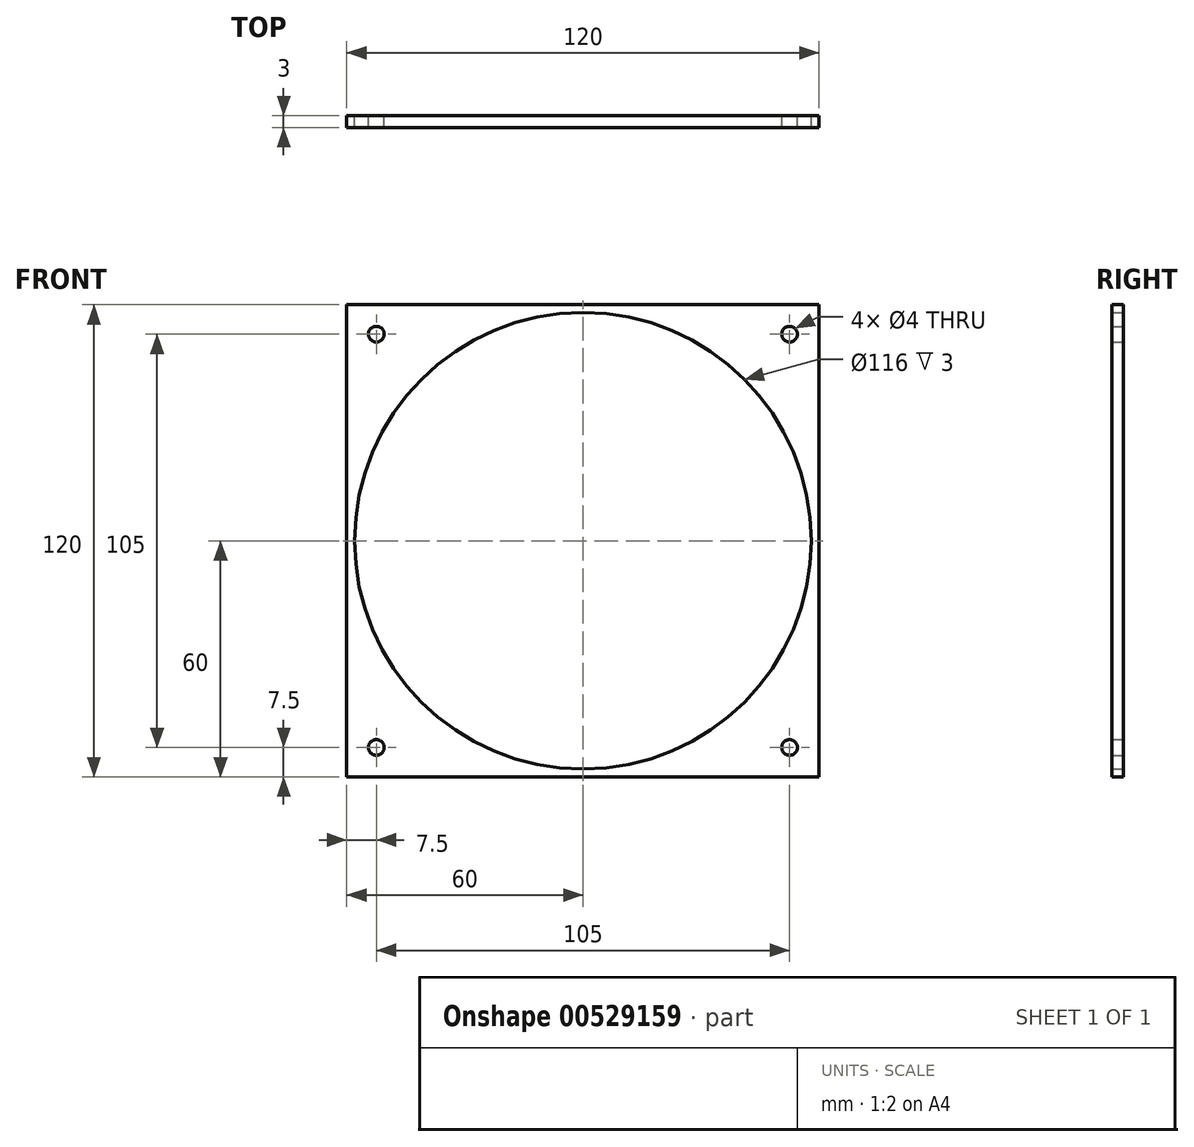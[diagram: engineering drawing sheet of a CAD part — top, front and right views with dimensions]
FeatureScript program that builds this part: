
annotation { "Feature Type Name" : "Feature", "Feature Type Description" : "" }
export const myFeature = defineFeature(function(context is Context, id is Id, definition is map)
    precondition{}
    {
        {
            var Q0;
            Q0=qCreatedBy(makeId("Front.planeOp"),FACE);
            var sketch = newSketch(context, id + "F0", { "sketchPlane" : qUnion([Q0])});
            skLineSegment(sketch, "E0.bottom", {"start": v(60, -60) * mm, "end": v(-60, -60) * mm});
            skLineSegment(sketch, "E0.top", {"start": v(60, 60) * mm, "end": v(-60, 60) * mm});
            skLineSegment(sketch, "E0.left", {"start": v(60, -60) * mm, "end": v(60, 60) * mm});
            skLineSegment(sketch, "E0.right", {"start": v(-60, -60) * mm, "end": v(-60, 60) * mm});
            skPoint(sketch, "E0.middle", {"position": v(0, 0) * mm});
            skLineSegment(sketch, "E1", {"start": v(-66.26, 54.5) * mm, "end": v(67.7, 54.5) * mm, "construction": true});
            skLineSegment(sketch, "E2", {"start": v(-54.5, 62.67) * mm, "end": v(-54.5, -64.31) * mm, "construction": true});
            skLineSegment(sketch, "E3", {"start": v(0, 63.39) * mm, "end": v(0, -62.98) * mm, "construction": true});
            skPoint(sketch, "E3.startSnap0", {"position": v(0, 60) * mm});
            skLineSegment(sketch, "E4", {"start": v(-62.77, 0) * mm, "end": v(61.96, 0) * mm, "construction": true});
            skPoint(sketch, "E4.startSnap0", {"position": v(-60, 0) * mm});
            skLineSegment(sketch, "E5.MirrorCS", {"start": v(-66.26, -54.5) * mm, "end": v(67.7, -54.5) * mm, "construction": true});
            skLineSegment(sketch, "E6.MirrorCS", {"start": v(54.5, 62.67) * mm, "end": v(54.5, -64.31) * mm, "construction": true});
            skCircle(sketch, "E7", {"center": v(-52.5, 52.5) * mm, "radius": 2 * mm});
            skCircle(sketch, "E8.MirrorC", {"center": v(52.5, 52.5) * mm, "radius": 2 * mm});
            skCircle(sketch, "E9.MirrorC", {"center": v(-52.5, -52.5) * mm, "radius": 2 * mm});
            skCircle(sketch, "E10.MirrorC", {"center": v(52.5, -52.5) * mm, "radius": 2 * mm});
            skCircle(sketch, "E11", {"center": v(0, 0) * mm, "radius": 58 * mm});
            skSolve(sketch);
        }
        {
            var Q0;
            Q0=makeQuery(id+"F0.imprint","IMPRINT",FACE,{"disambiguationData":[TD([[makeQuery(id+"F0.imprint","IMPRINT",EDGE,{"derivedFrom":sQuery(id+"F0.wireOp",EDGE,"E0.bottom")}),-1.0]])]});
            extrude(context, id + "F1", {"entities" : qUnion([Q0]), "depth" : 3 * mm, "offsetDistance" : 25 * mm});
        }
    });
